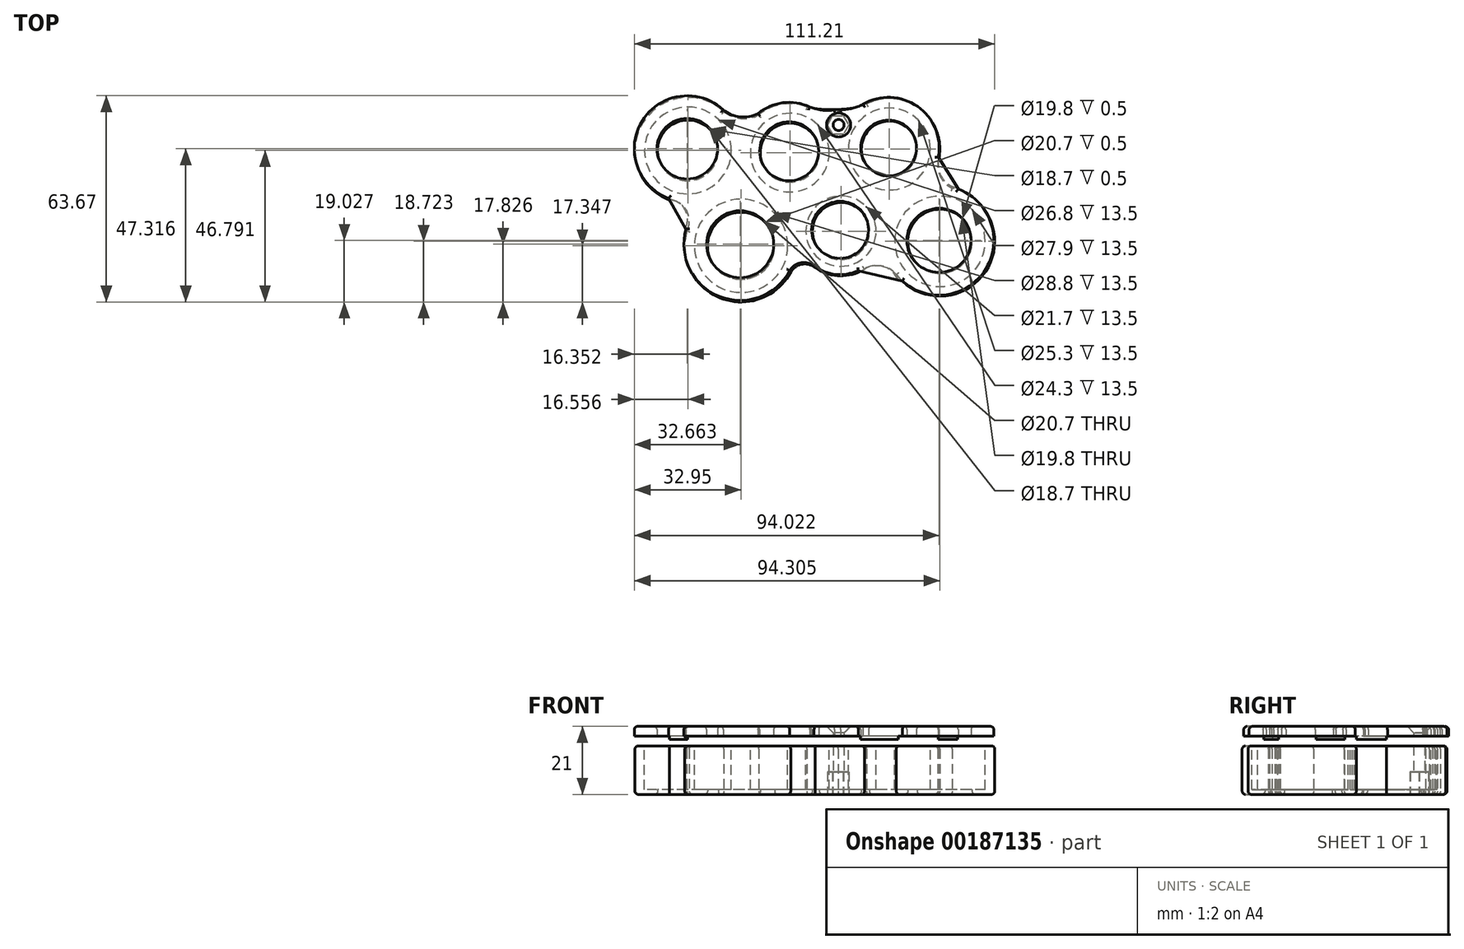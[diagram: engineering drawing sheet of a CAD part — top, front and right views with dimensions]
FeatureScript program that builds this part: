
annotation { "Feature Type Name" : "Feature", "Feature Type Description" : "" }
export const myFeature = defineFeature(function(context is Context, id is Id, definition is map)
    precondition{}
    {
        {
            var Q0;
            Q0=qCreatedBy(makeId("Top.planeOp"),FACE);
            var sketch = newSketch(context, id + "F0", { "sketchPlane" : qUnion([Q0])});
            skArc(sketch, "E0", {"start": v(-18.22, 23.12) * mm, "mid": v(-43.25, 19.71) * mm, "end": v(-35.08, -4.19) * mm});
            skArc(sketch, "E1", {"start": v(7.41, 24.56) * mm, "mid": v(-0.37, 25.32) * mm, "end": v(-7.48, 22.09) * mm});
            skArc(sketch, "E2", {"start": v(48.15, 8.81) * mm, "mid": v(42.1, 24.06) * mm, "end": v(25.77, 25.48) * mm});
            skArc(sketch, "E3", {"start": v(9.86, -25.02) * mm, "mid": v(17.41, -27.58) * mm, "end": v(25.12, -25.54) * mm});
            skArc(sketch, "E4", {"start": v(34.96, -27.17) * mm, "mid": v(62.62, -26.1) * mm, "end": v(52.17, -0.47) * mm});
            skArc(sketch, "E5", {"start": v(-29.65, -13.66) * mm, "mid": v(-19.4, -34.43) * mm, "end": v(2.37, -26.49) * mm});
            skArc(sketch, "E6", {"start": v(-29.65, -13.66) * mm, "mid": v(-29.77, -7.44) * mm, "end": v(-35.08, -4.19) * mm});
            skArc(sketch, "E7", {"start": v(-18.22, 23.12) * mm, "mid": v(-13.01, 20.97) * mm, "end": v(-7.48, 22.09) * mm});
            skArc(sketch, "E8", {"start": v(48.15, 8.81) * mm, "mid": v(48.38, 3.4) * mm, "end": v(52.17, -0.47) * mm});
            skArc(sketch, "E9", {"start": v(34.96, -27.17) * mm, "mid": v(30.34, -24.58) * mm, "end": v(25.12, -25.54) * mm});
            skArc(sketch, "E10", {"start": v(9.86, -25.02) * mm, "mid": v(5.77, -24) * mm, "end": v(2.37, -26.49) * mm});
            skCircle(sketch, "E11", {"center": v(-29.33, 11.12) * mm, "radius": 9.35 * mm});
            skCircle(sketch, "E12", {"center": v(-12.94, -18.32) * mm, "radius": 10.35 * mm});
            skCircle(sketch, "E13", {"center": v(2.1, 10.43) * mm, "radius": 9.1 * mm});
            skCircle(sketch, "E14", {"center": v(17.88, -13.8) * mm, "radius": 8.8 * mm});
            skCircle(sketch, "E15", {"center": v(32.79, 11.55) * mm, "radius": 8.6 * mm});
            skCircle(sketch, "E16", {"center": v(48.42, -16.95) * mm, "radius": 9.9 * mm});
            skPoint(sketch, "E17", {"position": v(17.46, 2.98) * mm});
            skPoint(sketch, "E18.orphan", {"position": v(17.45, 10.99) * mm});
            skPoint(sketch, "E19.orphan", {"position": v(25.33, -1.12) * mm});
            skPoint(sketch, "E20.trimOffspring.end.orphan", {"position": v(10, -1.68) * mm});
            skPoint(sketch, "E21.center.orphan", {"position": v(16.6, 25.02) * mm});
            skCircle(sketch, "E22", {"center": v(17.16, 18.98) * mm, "radius": 1.7 * mm});
            skArc(sketch, "E23", {"start": v(-7.48, 22.09) * mm, "mid": v(-0.37, 25.32) * mm, "end": v(7.41, 24.56) * mm});
            skCircle(sketch, "E24", {"center": v(32.79, 11.55) * mm, "radius": 12.5 * mm, "construction": true});
            skCircle(sketch, "E25", {"center": v(2.1, 10.43) * mm, "radius": 12.5 * mm, "construction": true});
            skLineSegment(sketch, "E26", {"start": v(2.1, 10.43) * mm, "end": v(32.79, 11.55) * mm, "construction": true});
            skLineSegment(sketch, "E27", {"start": v(17.45, 10.99) * mm, "end": v(16.75, 30.14) * mm, "construction": true});
            skArc(sketch, "E28", {"start": v(12.82, 21.07) * mm, "mid": v(15.08, 14.64) * mm, "end": v(21.5, 16.92) * mm, "construction": true});
            skArc(sketch, "E29", {"start": v(16.58, 23.76) * mm, "mid": v(16.98, 23.79) * mm, "end": v(17.38, 23.79) * mm});
            skArc(sketch, "E30", {"start": v(16.98, 23.79) * mm, "mid": v(21.46, 24.18) * mm, "end": v(25.77, 25.48) * mm});
            skArc(sketch, "E31", {"start": v(7.41, 24.56) * mm, "mid": v(12.16, 23.78) * mm, "end": v(16.98, 23.79) * mm});
            skArc(sketch, "E32.trimOffspring", {"start": v(17.38, 23.79) * mm, "mid": v(16.98, 23.79) * mm, "end": v(16.58, 23.76) * mm, "construction": true});
            skSolve(sketch);
        }
        {
            var Q0;
            Q0=makeQuery(id+"F0.imprint","IMPRINT",FACE,{"disambiguationData":[TD([[makeQuery(id+"F0.imprint","IMPRINT",EDGE,{"derivedFrom":sQuery(id+"F0.wireOp",EDGE,"E0")}),1.0]])]});
            extrude(context, id + "F1", {"entities" : qUnion([Q0]), "depth" : 15 * mm});
        }
        {
            var Q0;
            Q0=qCreatedBy(makeId("Top.planeOp"),FACE);
            cPlane(context, id + "F2", {"entities" : qUnion([Q0]), "cplaneType" : CPlaneType.OFFSET, "offset" : 18 * mm, "width" : 150 * mm, "height" : 150 * mm});
        }
        {
            var Q0;
            Q0=makeQuery(id+"F1.opExtrude","CAP_FACE",FACE,{"disambiguationData":[OSD([sQuery(id+"F0.wireOp",EDGE,"E0"),sQuery(id+"F0.wireOp",EDGE,"E1"),sQuery(id+"F0.wireOp",EDGE,"E2"),sQuery(id+"F0.wireOp",EDGE,"E3"),sQuery(id+"F0.wireOp",EDGE,"E4"),sQuery(id+"F0.wireOp",EDGE,"E5"),sQuery(id+"F0.wireOp",EDGE,"E6"),sQuery(id+"F0.wireOp",EDGE,"E7"),sQuery(id+"F0.wireOp",EDGE,"E8"),sQuery(id+"F0.wireOp",EDGE,"E9"),sQuery(id+"F0.wireOp",EDGE,"E10"),sQuery(id+"F0.wireOp",EDGE,"cmuSQvfR-1LlV-bjM8-RssA-lsbDypLqzE8I"),sQuery(id+"F0.wireOp",EDGE,"E21"),sQuery(id+"F0.wireOp",EDGE,"E11"),sQuery(id+"F0.wireOp",EDGE,"E12"),sQuery(id+"F0.wireOp",EDGE,"E13"),sQuery(id+"F0.wireOp",EDGE,"E14"),sQuery(id+"F0.wireOp",EDGE,"E15"),sQuery(id+"F0.wireOp",EDGE,"E16")])],"isStart":false});
            var sketch = newSketch(context, id + "F3", { "sketchPlane" : qUnion([Q0])});
            skCircle(sketch, "E33", {"center": v(-29.33, 11.12) * mm, "radius": 13.4 * mm});
            skCircle(sketch, "E34", {"center": v(-12.94, -18.32) * mm, "radius": 14.4 * mm});
            skCircle(sketch, "E35", {"center": v(17.88, -13.8) * mm, "radius": 10.85 * mm});
            skCircle(sketch, "E36", {"center": v(2.1, 10.43) * mm, "radius": 12.15 * mm});
            skCircle(sketch, "E37", {"center": v(32.79, 11.55) * mm, "radius": 12.65 * mm});
            skCircle(sketch, "E38", {"center": v(48.42, -16.95) * mm, "radius": 13.95 * mm});
            skSolve(sketch);
        }
        {
            var Q0;
            Q0=makeQuery(id+"F3.imprint","IMPRINT",FACE,{"disambiguationData":[TD([[makeQuery(id+"F3.imprint","IMPRINT",EDGE,{"derivedFrom":sQuery(id+"F3.wireOp",EDGE,"E33")}),1.0]])]});
            var Q1;
            Q1=makeQuery(id+"F3.imprint","IMPRINT",FACE,{"disambiguationData":[TD([[makeQuery(id+"F3.imprint","IMPRINT",EDGE,{"derivedFrom":sQuery(id+"F3.wireOp",EDGE,"E36")}),1.0]])]});
            var Q2;
            Q2=makeQuery(id+"F3.imprint","IMPRINT",FACE,{"disambiguationData":[TD([[makeQuery(id+"F3.imprint","IMPRINT",EDGE,{"derivedFrom":sQuery(id+"F3.wireOp",EDGE,"E37")}),1.0]])]});
            var Q3;
            Q3=makeQuery(id+"F3.imprint","IMPRINT",FACE,{"disambiguationData":[TD([[makeQuery(id+"F3.imprint","IMPRINT",EDGE,{"derivedFrom":sQuery(id+"F3.wireOp",EDGE,"E35")}),1.0]])]});
            var Q4;
            Q4=makeQuery(id+"F3.imprint","IMPRINT",FACE,{"disambiguationData":[TD([[makeQuery(id+"F3.imprint","IMPRINT",EDGE,{"derivedFrom":sQuery(id+"F3.wireOp",EDGE,"E34")}),1.0]])]});
            var Q5;
            Q5=makeQuery(id+"F3.imprint","IMPRINT",FACE,{"disambiguationData":[TD([[makeQuery(id+"F3.imprint","IMPRINT",EDGE,{"derivedFrom":sQuery(id+"F3.wireOp",EDGE,"E38")}),1.0]])]});
            extrude(context, id + "F4", {"entities" : qUnion([Q0, Q1, Q2, Q3, Q4, Q5]), "operationType" : NewBodyOperationType.REMOVE, "oppositeDirection" : true, "depth" : 13.5 * mm});
        }
        {
            var Q0;
            Q0=qCreatedBy(makeId("Top.planeOp"),FACE);
            var sketch = newSketch(context, id + "F5", { "sketchPlane" : qUnion([Q0])});
            skPoint(sketch, "E39", {"position": v(16.98, 18.98) * mm});
            skCircle(sketch, "E40.cCircle", {"center": v(16.98, 18.98) * mm, "radius": 2.86 * mm, "construction": true});
            skLineSegment(sketch, "E40.0", {"start": v(18.58, 21.87) * mm, "end": v(20.28, 19.04) * mm});
            skLineSegment(sketch, "E40.1", {"start": v(20.28, 19.04) * mm, "end": v(18.67, 16.15) * mm});
            skLineSegment(sketch, "E40.2", {"start": v(18.67, 16.15) * mm, "end": v(15.37, 16.1) * mm});
            skLineSegment(sketch, "E40.3", {"start": v(15.37, 16.1) * mm, "end": v(13.68, 18.93) * mm});
            skLineSegment(sketch, "E40.4", {"start": v(13.68, 18.93) * mm, "end": v(15.28, 21.81) * mm});
            skLineSegment(sketch, "E40.5", {"start": v(15.28, 21.81) * mm, "end": v(18.58, 21.87) * mm});
            skPoint(sketch, "E40.0.midPoint", {"position": v(19.43, 20.45) * mm});
            skPoint(sketch, "E41", {"position": v(17.16, 18.98) * mm});
            skSolve(sketch);
        }
        {
            var Q0;
            Q0=makeQuery(id+"F5.imprint","IMPRINT",FACE,{"disambiguationData":[TD([[makeQuery(id+"F5.imprint","IMPRINT",EDGE,{"derivedFrom":sQuery(id+"F5.wireOp",EDGE,"E40.0")}),-1.0]])]});
            extrude(context, id + "F6", {"entities" : qUnion([Q0]), "operationType" : NewBodyOperationType.REMOVE, "depth" : 7 * mm});
        }
        {
            var Q0;
            Q0=qCreatedBy(id+"F2.planeOp",FACE);
            var sketch = newSketch(context, id + "F7", { "sketchPlane" : qUnion([Q0])});
            skArc(sketch, "E42", {"start": v(-18.43, 23.64) * mm, "mid": v(-43.45, 20.24) * mm, "end": v(-35.28, -3.66) * mm});
            skArc(sketch, "E43", {"start": v(7.53, 24.87) * mm, "mid": v(-0.4, 25.79) * mm, "end": v(-7.7, 22.52) * mm});
            skArc(sketch, "E44", {"start": v(47.94, 9.16) * mm, "mid": v(41.9, 24.4) * mm, "end": v(25.57, 25.83) * mm});
            skArc(sketch, "E45", {"start": v(9.59, -24.63) * mm, "mid": v(17.14, -27.2) * mm, "end": v(24.85, -25.15) * mm});
            skArc(sketch, "E46", {"start": v(34.68, -26.87) * mm, "mid": v(62.34, -25.8) * mm, "end": v(51.88, -0.16) * mm});
            skArc(sketch, "E47", {"start": v(-29.94, -13.18) * mm, "mid": v(-19.68, -33.95) * mm, "end": v(2.08, -26) * mm});
            skArc(sketch, "E48", {"start": v(-29.94, -13.18) * mm, "mid": v(-30, -6.96) * mm, "end": v(-35.28, -3.66) * mm});
            skArc(sketch, "E49", {"start": v(-18.43, 23.64) * mm, "mid": v(-13.23, 21.45) * mm, "end": v(-7.7, 22.52) * mm});
            skArc(sketch, "E50", {"start": v(47.94, 9.16) * mm, "mid": v(48.13, 3.75) * mm, "end": v(51.88, -0.16) * mm});
            skArc(sketch, "E51", {"start": v(34.68, -26.87) * mm, "mid": v(30.07, -24.23) * mm, "end": v(24.85, -25.15) * mm});
            skArc(sketch, "E52", {"start": v(9.59, -24.63) * mm, "mid": v(5.51, -23.57) * mm, "end": v(2.08, -26) * mm});
            skCircle(sketch, "E53", {"center": v(-29.54, 11.65) * mm, "radius": 9.35 * mm});
            skCircle(sketch, "E54", {"center": v(-13.23, -17.84) * mm, "radius": 10.35 * mm});
            skCircle(sketch, "E55", {"center": v(1.9, 10.86) * mm, "radius": 9.1 * mm});
            skCircle(sketch, "E56", {"center": v(17.6, -13.4) * mm, "radius": 8.8 * mm});
            skCircle(sketch, "E57", {"center": v(32.59, 11.9) * mm, "radius": 8.6 * mm});
            skCircle(sketch, "E58", {"center": v(48.13, -16.64) * mm, "radius": 9.9 * mm});
            skLineSegment(sketch, "E59", {"start": v(-29.94, -13.18) * mm, "end": v(-35.28, -3.66) * mm});
            skArc(sketch, "E60", {"start": v(-30.11, -12.87) * mm, "mid": v(-30.27, -7.1) * mm, "end": v(-35.1, -3.97) * mm});
            skArc(sketch, "E61", {"start": v(34.2, -26.79) * mm, "mid": v(30.02, -24.52) * mm, "end": v(25.32, -25.23) * mm});
            skLineSegment(sketch, "E62", {"start": v(54.05, -0.81) * mm, "end": v(47.94, 9.16) * mm});
            skArc(sketch, "E63", {"start": v(48.15, 8.83) * mm, "mid": v(48.9, 2.9) * mm, "end": v(53.84, -0.48) * mm});
            skArc(sketch, "E64", {"start": v(35.61, -28.94) * mm, "mid": v(30.44, -24.61) * mm, "end": v(23.89, -26.18) * mm});
            skLineSegment(sketch, "E65", {"start": v(23.2, -26.02) * mm, "end": v(36.86, -29.23) * mm});
            skPoint(sketch, "E66.center.orphan", {"position": v(16.55, 25.35) * mm});
            skCircle(sketch, "E67", {"center": v(17.16, 18.98) * mm, "radius": 1.7 * mm});
            skArc(sketch, "E68", {"start": v(7.53, 24.87) * mm, "mid": v(7.9, 24.72) * mm, "end": v(8.28, 24.55) * mm});
            skArc(sketch, "E69", {"start": v(25.57, 25.83) * mm, "mid": v(25.13, 25.6) * mm, "end": v(24.7, 25.36) * mm});
            skArc(sketch, "E70", {"start": v(12.9, 21.22) * mm, "mid": v(17.7, 14.2) * mm, "end": v(20.8, 22.12) * mm, "construction": true});
            skArc(sketch, "E71", {"start": v(15.82, 23.6) * mm, "mid": v(16.8, 23.78) * mm, "end": v(17.79, 23.75) * mm});
            skArc(sketch, "E72", {"start": v(16.89, 23.78) * mm, "mid": v(21.38, 24.15) * mm, "end": v(25.57, 25.83) * mm});
            skArc(sketch, "E73", {"start": v(7.53, 24.87) * mm, "mid": v(12.12, 23.57) * mm, "end": v(16.89, 23.78) * mm});
            skArc(sketch, "E74.trimOffspring", {"start": v(17.79, 23.75) * mm, "mid": v(16.8, 23.78) * mm, "end": v(15.82, 23.6) * mm, "construction": true});
            skSolve(sketch);
        }
        {
            var Q0;
            Q0=qSketchRegion(id+"F7",true);
            extrude(context, id + "F8", {"entities" : qUnion([Q0]), "depth" : 3 * mm});
        }
        {
            var Q0;
            {var subQ0=sQuery(id+"F7.wireOp",EDGE,"abFJn2rG-QnjB-3oZD-kfx5-oWbmogYZg01U");Q0=makeQuery(id+"F7.imprint","IMPRINT",FACE,{"disambiguationData":[TD([[makeQuery(id+"F7.imprint","IMPRINT",EDGE,{"derivedFrom":subQ0}),1.0]])]});}
            var Q1;
            {var subQ0=sQuery(id+"F7.wireOp",EDGE,"E60");Q1=makeQuery(id+"F7.imprint","IMPRINT",FACE,{"disambiguationData":[TD([[makeQuery(id+"F7.imprint","IMPRINT",EDGE,{"derivedFrom":subQ0}),1.0]])]});}
            var Q2;
            {var subQ0=sQuery(id+"F7.wireOp",EDGE,"E61");Q2=makeQuery(id+"F7.imprint","IMPRINT",FACE,{"disambiguationData":[TD([[makeQuery(id+"F7.imprint","IMPRINT",EDGE,{"derivedFrom":subQ0}),1.0]])]});}
            var Q3;
            {var subQ0=sQuery(id+"F7.wireOp",EDGE,"E63");Q3=makeQuery(id+"F7.imprint","IMPRINT",FACE,{"disambiguationData":[TD([[makeQuery(id+"F7.imprint","IMPRINT",EDGE,{"derivedFrom":subQ0}),1.0]])]});}
            var Q4;
            {var subQ1=sQuery(id+"F7.wireOp",EDGE,"E64");var subQ3=makeQuery(id+"F7.imprint","IMPRINT",VERTEX,{"disambiguationData":[OD(0.0)],"derivedFrom":subQ1});Q4=makeQuery(id+"F7.imprint","IMPRINT",FACE,{"disambiguationData":[TD([[makeQuery(id+"F7.imprint","IMPRINT",EDGE,{"disambiguationData":[TD([[subQ3,-1.0]])],"derivedFrom":subQ1}),1.0]])]});}
            extrude(context, id + "F9", {"entities" : qUnion([Q0, Q1, Q2, Q3, Q4]), "operationType" : NewBodyOperationType.ADD, "oppositeDirection" : true, "depth" : 1 * mm});
        }
        {
            var Q0;
            Q0=makeQuery(id+"F1.opExtrude","CAP_EDGE",EDGE,{"disambiguationData":[OSD([sQuery(id+"F0.wireOp",EDGE,"E2")])],"isStart":true});
            var Q1;
            Q1=makeQuery(id+"F1.opExtrude","CAP_EDGE",EDGE,{"disambiguationData":[OSD([sQuery(id+"F0.wireOp",EDGE,"cmuSQvfR-1LlV-bjM8-RssA-lsbDypLqzE8I")])],"isStart":true});
            var Q2;
            Q2=makeQuery(id+"F1.opExtrude","CAP_EDGE",EDGE,{"disambiguationData":[OSD([sQuery(id+"F0.wireOp",EDGE,"E1")])],"isStart":true});
            var Q3;
            Q3=makeQuery(id+"F1.opExtrude","CAP_EDGE",EDGE,{"disambiguationData":[OSD([sQuery(id+"F0.wireOp",EDGE,"E7")])],"isStart":true});
            var Q4;
            Q4=makeQuery(id+"F1.opExtrude","CAP_EDGE",EDGE,{"disambiguationData":[OSD([sQuery(id+"F0.wireOp",EDGE,"E0")])],"isStart":true});
            var Q5;
            Q5=makeQuery(id+"F1.opExtrude","CAP_EDGE",EDGE,{"disambiguationData":[OSD([sQuery(id+"F0.wireOp",EDGE,"E6")])],"isStart":true});
            var Q6;
            Q6=makeQuery(id+"F1.opExtrude","CAP_EDGE",EDGE,{"disambiguationData":[OSD([sQuery(id+"F0.wireOp",EDGE,"E5")])],"isStart":true});
            var Q7;
            Q7=makeQuery(id+"F1.opExtrude","CAP_EDGE",EDGE,{"disambiguationData":[OSD([sQuery(id+"F0.wireOp",EDGE,"E10")])],"isStart":true});
            var Q8;
            Q8=makeQuery(id+"F1.opExtrude","CAP_EDGE",EDGE,{"disambiguationData":[OSD([sQuery(id+"F0.wireOp",EDGE,"E3")])],"isStart":true});
            var Q9;
            Q9=makeQuery(id+"F1.opExtrude","CAP_EDGE",EDGE,{"disambiguationData":[OSD([sQuery(id+"F0.wireOp",EDGE,"E9")])],"isStart":true});
            var Q10;
            Q10=makeQuery(id+"F1.opExtrude","CAP_EDGE",EDGE,{"disambiguationData":[OSD([sQuery(id+"F0.wireOp",EDGE,"E4")])],"isStart":true});
            var Q11;
            Q11=makeQuery(id+"F1.opExtrude","CAP_EDGE",EDGE,{"disambiguationData":[OSD([sQuery(id+"F0.wireOp",EDGE,"E8")])],"isStart":true});
            var Q12;
            Q12=makeQuery(id+"F1.opExtrude","CAP_EDGE",EDGE,{"disambiguationData":[OSD([sQuery(id+"F0.wireOp",EDGE,"E2")])],"isStart":false});
            var Q13;
            Q13=makeQuery(id+"F1.opExtrude","CAP_EDGE",EDGE,{"disambiguationData":[OSD([sQuery(id+"F0.wireOp",EDGE,"cmuSQvfR-1LlV-bjM8-RssA-lsbDypLqzE8I")])],"isStart":false});
            var Q14;
            Q14=makeQuery(id+"F1.opExtrude","CAP_EDGE",EDGE,{"disambiguationData":[OSD([sQuery(id+"F0.wireOp",EDGE,"E1")])],"isStart":false});
            var Q15;
            Q15=makeQuery(id+"F1.opExtrude","CAP_EDGE",EDGE,{"disambiguationData":[OSD([sQuery(id+"F0.wireOp",EDGE,"E7")])],"isStart":false});
            var Q16;
            Q16=makeQuery(id+"F1.opExtrude","CAP_EDGE",EDGE,{"disambiguationData":[OSD([sQuery(id+"F0.wireOp",EDGE,"E0")])],"isStart":false});
            var Q17;
            Q17=makeQuery(id+"F1.opExtrude","CAP_EDGE",EDGE,{"disambiguationData":[OSD([sQuery(id+"F0.wireOp",EDGE,"E6")])],"isStart":false});
            var Q18;
            Q18=makeQuery(id+"F1.opExtrude","CAP_EDGE",EDGE,{"disambiguationData":[OSD([sQuery(id+"F0.wireOp",EDGE,"E5")])],"isStart":false});
            var Q19;
            Q19=makeQuery(id+"F1.opExtrude","CAP_EDGE",EDGE,{"disambiguationData":[OSD([sQuery(id+"F0.wireOp",EDGE,"E10")])],"isStart":false});
            var Q20;
            Q20=makeQuery(id+"F1.opExtrude","CAP_EDGE",EDGE,{"disambiguationData":[OSD([sQuery(id+"F0.wireOp",EDGE,"E3")])],"isStart":false});
            var Q21;
            Q21=makeQuery(id+"F1.opExtrude","CAP_EDGE",EDGE,{"disambiguationData":[OSD([sQuery(id+"F0.wireOp",EDGE,"E9")])],"isStart":false});
            var Q22;
            Q22=makeQuery(id+"F1.opExtrude","CAP_EDGE",EDGE,{"disambiguationData":[OSD([sQuery(id+"F0.wireOp",EDGE,"E4")])],"isStart":false});
            var Q23;
            Q23=makeQuery(id+"F1.opExtrude","CAP_EDGE",EDGE,{"disambiguationData":[OSD([sQuery(id+"F0.wireOp",EDGE,"E8")])],"isStart":false});
            var Q24;
            Q24=makeQuery(id+"F1.opExtrude","CAP_EDGE",EDGE,{"disambiguationData":[OSD([sQuery(id+"F0.wireOp",EDGE,"RsfDVoeq-88MK-O4fM-M0ip-vEhRewOvGteJ")])],"isStart":true});
            var Q25;
            Q25=makeQuery(id+"F1.opExtrude","CAP_EDGE",EDGE,{"disambiguationData":[OSD([sQuery(id+"F0.wireOp",EDGE,"RsfDVoeq-88MK-O4fM-M0ip-vEhRewOvGteJ")])],"isStart":false});
            var Q26;
            Q26=makeQuery(id+"F1.opExtrude","CAP_EDGE",EDGE,{"disambiguationData":[OSD([sQuery(id+"F0.wireOp",EDGE,"cKg1eJ1H-dBtz-pCOY-6ZJL-w3ln1pFaWfeZ")])],"isStart":false});
            var Q27;
            Q27=makeQuery(id+"F1.opExtrude","CAP_EDGE",EDGE,{"disambiguationData":[OSD([sQuery(id+"F0.wireOp",EDGE,"cKg1eJ1H-dBtz-pCOY-6ZJL-w3ln1pFaWfeZ")])],"isStart":true});
            var Q28;
            Q28=makeQuery(id+"F1.opExtrude","CAP_EDGE",EDGE,{"disambiguationData":[OSD([sQuery(id+"F0.wireOp",EDGE,"E13")])],"isStart":true});
            var Q29;
            Q29=makeQuery(id+"F1.opExtrude","CAP_EDGE",EDGE,{"disambiguationData":[OSD([sQuery(id+"F0.wireOp",EDGE,"E15")])],"isStart":true});
            var Q30;
            Q30=makeQuery(id+"F1.opExtrude","CAP_EDGE",EDGE,{"disambiguationData":[OSD([sQuery(id+"F0.wireOp",EDGE,"E16")])],"isStart":true});
            var Q31;
            Q31=makeQuery(id+"F1.opExtrude","CAP_EDGE",EDGE,{"disambiguationData":[OSD([sQuery(id+"F0.wireOp",EDGE,"E14")])],"isStart":true});
            var Q32;
            Q32=makeQuery(id+"F1.opExtrude","CAP_EDGE",EDGE,{"disambiguationData":[OSD([sQuery(id+"F0.wireOp",EDGE,"E12")])],"isStart":true});
            var Q33;
            Q33=makeQuery(id+"F1.opExtrude","CAP_EDGE",EDGE,{"disambiguationData":[OSD([sQuery(id+"F0.wireOp",EDGE,"E11")])],"isStart":true});
            var Q34;
            Q34=makeQuery(id+"F1.opExtrude","CAP_EDGE",EDGE,{"disambiguationData":[OSD([sQuery(id+"F0.wireOp",EDGE,"E23")])],"isStart":false});
            var Q35;
            Q35=makeQuery(id+"F1.opExtrude","CAP_EDGE",EDGE,{"disambiguationData":[OSD([sQuery(id+"F0.wireOp",EDGE,"E31")])],"isStart":false});
            var Q36;
            Q36=makeQuery(id+"F1.opExtrude","CAP_EDGE",EDGE,{"disambiguationData":[OSD([sQuery(id+"F0.wireOp",EDGE,"E30")])],"isStart":false});
            var Q37;
            Q37=makeQuery(id+"F1.opExtrude","CAP_EDGE",EDGE,{"disambiguationData":[OSD([sQuery(id+"F0.wireOp",EDGE,"E23")])],"isStart":true});
            var Q38;
            Q38=makeQuery(id+"F1.opExtrude","CAP_EDGE",EDGE,{"disambiguationData":[OSD([sQuery(id+"F0.wireOp",EDGE,"E31")])],"isStart":true});
            var Q39;
            Q39=makeQuery(id+"F1.opExtrude","CAP_EDGE",EDGE,{"disambiguationData":[OSD([sQuery(id+"F0.wireOp",EDGE,"E30")])],"isStart":true});
            fillet(context, id + "F10", {"entities" : qUnion([Q0, Q1, Q2, Q3, Q4, Q5, Q6, Q7, Q8, Q9, Q10, Q11, Q12, Q13, Q14, Q15, Q16, Q17, Q18, Q19, Q20, Q21, Q22, Q23, Q24, Q25, Q26, Q27, Q28, Q29, Q30, Q31, Q32, Q33, Q34, Q35, Q36, Q37, Q38, Q39]), "radius" : 1 * mm, "tangentPropagation" : true, "allowEdgeOverflow" : false});
        }
        {
            var Q0;
            Q0=makeQuery(id+"F8.opExtrude","CAP_EDGE",EDGE,{"disambiguationData":[OSD([sQuery(id+"F7.wireOp",EDGE,"E55")])],"isStart":false});
            var Q1;
            Q1=makeQuery(id+"F8.opExtrude","CAP_EDGE",EDGE,{"disambiguationData":[OSD([sQuery(id+"F7.wireOp",EDGE,"E53")])],"isStart":false});
            var Q2;
            Q2=makeQuery(id+"F8.opExtrude","CAP_EDGE",EDGE,{"disambiguationData":[OSD([sQuery(id+"F7.wireOp",EDGE,"E54")])],"isStart":false});
            var Q3;
            Q3=makeQuery(id+"F8.opExtrude","CAP_EDGE",EDGE,{"disambiguationData":[OSD([sQuery(id+"F7.wireOp",EDGE,"E56")])],"isStart":false});
            var Q4;
            Q4=makeQuery(id+"F8.opExtrude","CAP_EDGE",EDGE,{"disambiguationData":[OSD([sQuery(id+"F7.wireOp",EDGE,"E57")])],"isStart":false});
            var Q5;
            Q5=makeQuery(id+"F8.opExtrude","CAP_EDGE",EDGE,{"disambiguationData":[OSD([sQuery(id+"F7.wireOp",EDGE,"E58")])],"isStart":false});
            var Q6;
            Q6=makeQuery(id+"F8.opExtrude","CAP_EDGE",EDGE,{"disambiguationData":[OSD([sQuery(id+"F7.wireOp",EDGE,"E62")])],"isStart":false});
            var Q7;
            Q7=makeQuery(id+"F8.opExtrude","CAP_EDGE",EDGE,{"disambiguationData":[OSD([sQuery(id+"F7.wireOp",EDGE,"E46")])],"isStart":false});
            var Q8;
            Q8=makeQuery(id+"F8.opExtrude","CAP_EDGE",EDGE,{"disambiguationData":[OSD([sQuery(id+"F7.wireOp",EDGE,"E65")])],"isStart":false});
            var Q9;
            Q9=makeQuery(id+"F8.opExtrude","CAP_EDGE",EDGE,{"disambiguationData":[OSD([sQuery(id+"F7.wireOp",EDGE,"E45")])],"isStart":false});
            var Q10;
            Q10=makeQuery(id+"F8.opExtrude","CAP_EDGE",EDGE,{"disambiguationData":[OSD([sQuery(id+"F7.wireOp",EDGE,"E52")])],"isStart":false});
            var Q11;
            Q11=makeQuery(id+"F8.opExtrude","CAP_EDGE",EDGE,{"disambiguationData":[OSD([sQuery(id+"F7.wireOp",EDGE,"E47")])],"isStart":false});
            var Q12;
            Q12=makeQuery(id+"F8.opExtrude","CAP_EDGE",EDGE,{"disambiguationData":[OSD([sQuery(id+"F7.wireOp",EDGE,"E59")])],"isStart":false});
            var Q13;
            Q13=makeQuery(id+"F8.opExtrude","CAP_EDGE",EDGE,{"disambiguationData":[OSD([sQuery(id+"F7.wireOp",EDGE,"E42")])],"isStart":false});
            var Q14;
            Q14=makeQuery(id+"F8.opExtrude","CAP_EDGE",EDGE,{"disambiguationData":[OSD([sQuery(id+"F7.wireOp",EDGE,"E49")])],"isStart":false});
            var Q15;
            Q15=makeQuery(id+"F8.opExtrude","CAP_EDGE",EDGE,{"disambiguationData":[OSD([sQuery(id+"F7.wireOp",EDGE,"E43")])],"isStart":false});
            var Q16;
            Q16=makeQuery(id+"F8.opExtrude","CAP_EDGE",EDGE,{"disambiguationData":[OSD([sQuery(id+"F7.wireOp",EDGE,"69c1c0b9-9592-4324-a081-7276ba0f928f")])],"isStart":false});
            var Q17;
            Q17=makeQuery(id+"F8.opExtrude","CAP_EDGE",EDGE,{"disambiguationData":[OSD([sQuery(id+"F7.wireOp",EDGE,"E44")])],"isStart":false});
            var Q18;
            Q18=makeQuery(id+"F8.opExtrude","CAP_EDGE",EDGE,{"disambiguationData":[OSD([sQuery(id+"F7.wireOp",EDGE,"kM5ekBen-nXE2-MILf-Qjit-WzR8I1UkmNf8")])],"isStart":false});
            var Q19;
            Q19=makeQuery(id+"F8.opExtrude","CAP_EDGE",EDGE,{"disambiguationData":[OSD([sQuery(id+"F7.wireOp",EDGE,"l6xmWDMC-WJis-cdLo-k5yu-fUjOSxYiHxLJ")])],"isStart":false});
            var Q20;
            Q20=makeQuery(id+"F8.opExtrude","CAP_EDGE",EDGE,{"disambiguationData":[OSD([sQuery(id+"F7.wireOp",EDGE,"E71")])],"isStart":false});
            var Q21;
            Q21=makeQuery(id+"F8.opExtrude","CAP_EDGE",EDGE,{"disambiguationData":[OSD([sQuery(id+"F7.wireOp",EDGE,"E72")])],"isStart":false});
            var Q22;
            Q22=makeQuery(id+"F8.opExtrude","CAP_EDGE",EDGE,{"disambiguationData":[OSD([sQuery(id+"F7.wireOp",EDGE,"E73")])],"isStart":false});
            fillet(context, id + "F11", {"entities" : qUnion([Q0, Q1, Q2, Q3, Q4, Q5, Q6, Q7, Q8, Q9, Q10, Q11, Q12, Q13, Q14, Q15, Q16, Q17, Q18, Q19, Q20, Q21, Q22]), "radius" : 1 * mm, "tangentPropagation" : true, "allowEdgeOverflow" : false});
        }
        {
            var Q0;
            Q0=makeQuery(id+"F8.opExtrude","CAP_EDGE",EDGE,{"disambiguationData":[OSD([sQuery(id+"F7.wireOp",EDGE,"E67")])],"isStart":false});
            chamfer(context, id + "F12", {"entities" : qUnion([Q0]), "width" : 2 * mm, "tangentPropagation" : true});
        }
    });
